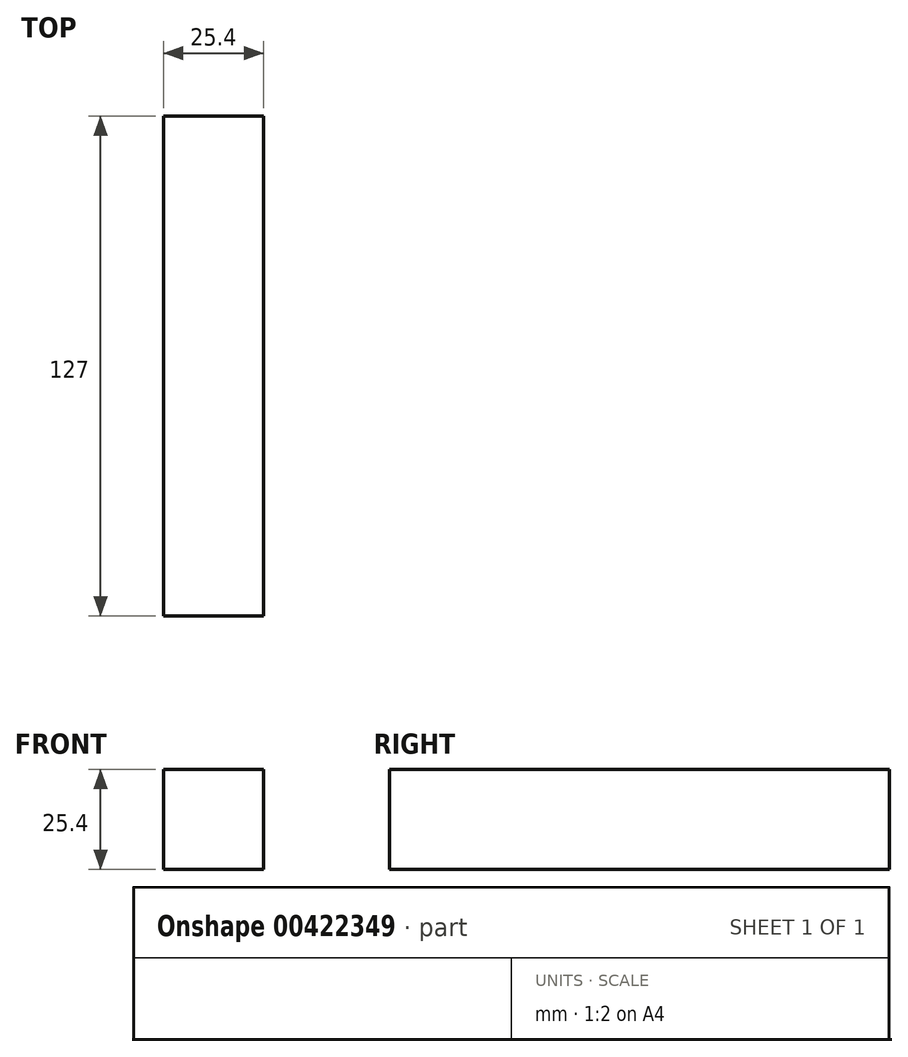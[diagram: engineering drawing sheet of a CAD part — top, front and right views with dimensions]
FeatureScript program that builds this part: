
annotation { "Feature Type Name" : "Feature", "Feature Type Description" : "" }
export const myFeature = defineFeature(function(context is Context, id is Id, definition is map)
    precondition{}
    {
        {
            var Q0;
            Q0=qCreatedBy(makeId("Front.planeOp"),FACE);
            var sketch = newSketch(context, id + "F0", { "sketchPlane" : qUnion([Q0])});
            skLineSegment(sketch, "E0.bottom", {"start": v(-10.98, 18.49) * mm, "end": v(14.42, 18.49) * mm});
            skLineSegment(sketch, "E0.top", {"start": v(-10.98, -6.91) * mm, "end": v(14.42, -6.91) * mm});
            skLineSegment(sketch, "E0.left", {"start": v(-10.98, 18.49) * mm, "end": v(-10.98, -6.91) * mm});
            skLineSegment(sketch, "E0.right", {"start": v(14.42, 18.49) * mm, "end": v(14.42, -6.91) * mm});
            skSolve(sketch);
        }
        {
            var Q0;
            Q0 = qSketchRegion(id + "F0", true);
            extrude(context, id + "F1", {"entities" : qUnion([Q0]), "depth" : 127 * mm});
        }
    });
